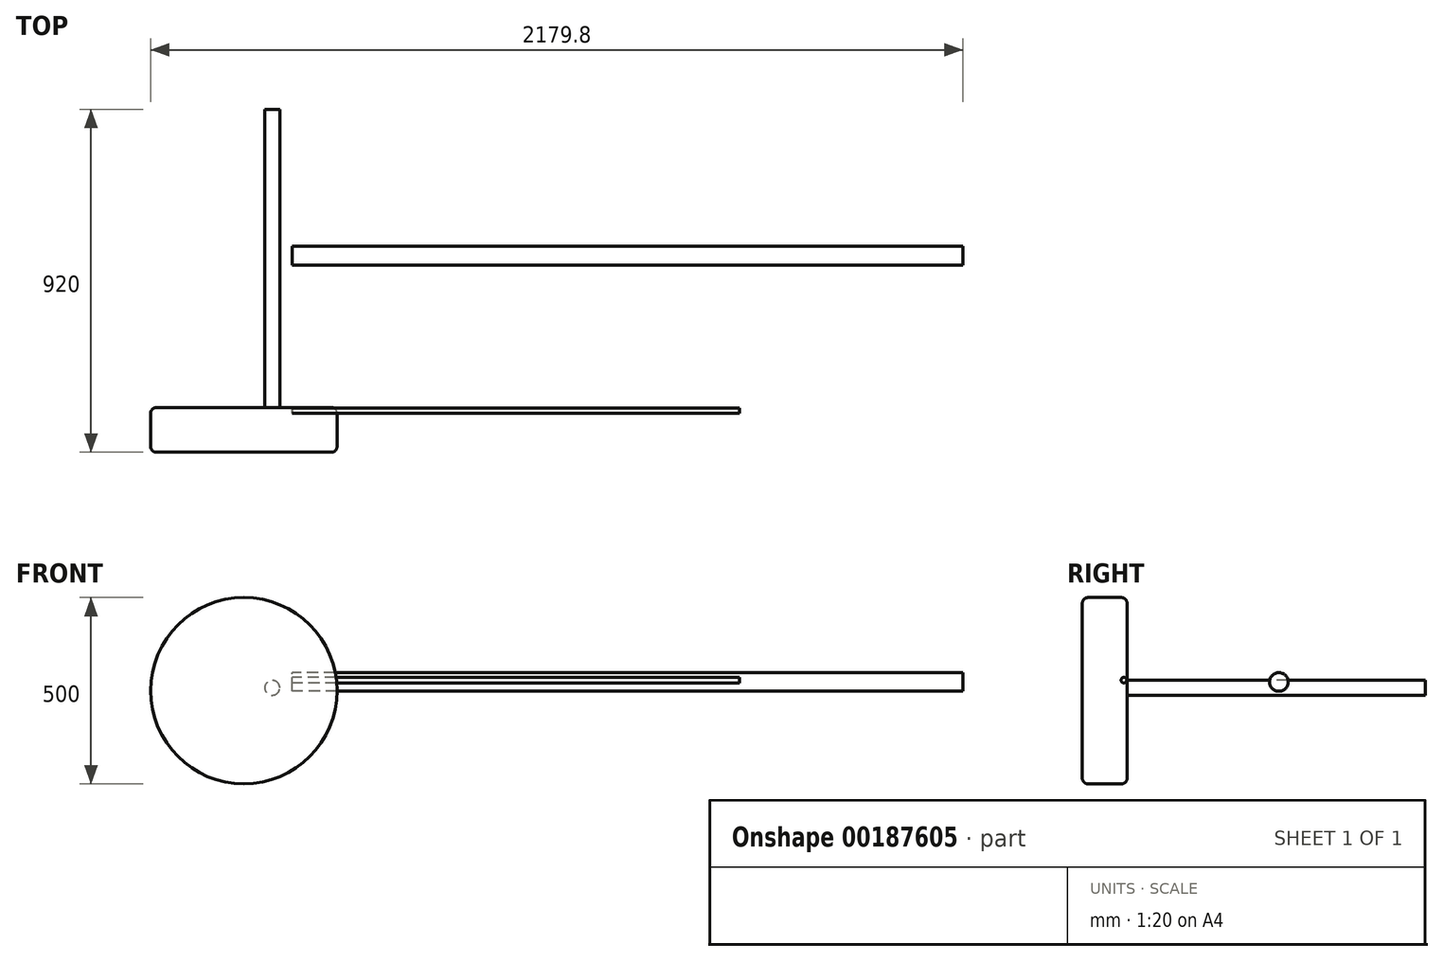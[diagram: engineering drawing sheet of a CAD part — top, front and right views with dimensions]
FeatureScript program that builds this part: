
annotation { "Feature Type Name" : "Feature", "Feature Type Description" : "" }
export const myFeature = defineFeature(function(context is Context, id is Id, definition is map)
    precondition{}
    {
        {
            var Q0;
            Q0=qCreatedBy(makeId("Front.planeOp"),FACE);
            var sketch = newSketch(context, id + "F0", { "sketchPlane" : qUnion([Q0])});
            skCircle(sketch, "E0", {"center": v(-129.8, -23.54) * mm, "radius": 250 * mm});
            skSolve(sketch);
        }
        {
            var Q0;
            Q0=makeQuery(id+"F0.imprint","IMPRINT",FACE,{"disambiguationData":[TD([[makeQuery(id+"F0.imprint","IMPRINT",EDGE,{"derivedFrom":sQuery(id+"F0.wireOp",EDGE,"E0")}),1.0]])]});
            extrude(context, id + "F1", {"entities" : qUnion([Q0]), "depth" : 120 * mm});
        }
        {
            var Q0;
            Q0=makeQuery(id+"F1.opExtrude","CAP_EDGE",EDGE,{"disambiguationData":[OSD([sQuery(id+"F0.wireOp",EDGE,"E0")])],"isStart":true});
            var Q1;
            Q1=makeQuery(id+"F1.opExtrude","SWEPT_FACE",FACE,{"disambiguationData":[OSD([sQuery(id+"F0.wireOp",EDGE,"E0")])]});
            fillet(context, id + "F2", {"entities" : qUnion([Q0, Q1]), "radius" : 15 * mm, "tangentPropagation" : true, "allowEdgeOverflow" : false});
        }
        {
            var Q0;
            Q0=qCreatedBy(makeId("Front.planeOp"),FACE);
            var sketch = newSketch(context, id + "F3", { "sketchPlane" : qUnion([Q0])});
            skCircle(sketch, "E1", {"center": v(-53.57, -15.6) * mm, "radius": 20 * mm});
            skSolve(sketch);
        }
        {
            var Q0;
            Q0=makeQuery(id+"F3.imprint","IMPRINT",FACE,{"disambiguationData":[TD([[makeQuery(id+"F3.imprint","IMPRINT",EDGE,{"derivedFrom":sQuery(id+"F3.wireOp",EDGE,"E1")}),1.0]])]});
            extrude(context, id + "F4", {"entities" : qUnion([Q0]), "oppositeDirection" : true, "depth" : 800 * mm});
        }
        {
            var Q0;
            Q0=qCreatedBy(makeId("Right.planeOp"),FACE);
            var sketch = newSketch(context, id + "F5", { "sketchPlane" : qUnion([Q0])});
            skCircle(sketch, "E2", {"center": v(-8.47, 4.92) * mm, "radius": 7.5 * mm});
            skSolve(sketch);
        }
        {
            var Q0;
            Q0=makeQuery(id+"F5.imprint","IMPRINT",FACE,{"disambiguationData":[TD([[makeQuery(id+"F5.imprint","IMPRINT",EDGE,{"derivedFrom":sQuery(id+"F5.wireOp",EDGE,"E2")}),1.0]])]});
            extrude(context, id + "F6", {"entities" : qUnion([Q0]), "depth" : 1200 * mm});
        }
        {
            var Q0;
            Q0=qCreatedBy(makeId("Right.planeOp"),FACE);
            var sketch = newSketch(context, id + "F7", { "sketchPlane" : qUnion([Q0])});
            skCircle(sketch, "E3", {"center": v(407.4, 0) * mm, "radius": 25 * mm});
            skSolve(sketch);
        }
        {
            var Q0;
            Q0=makeQuery(id+"F7.imprint","IMPRINT",FACE,{"disambiguationData":[TD([[makeQuery(id+"F7.imprint","IMPRINT",EDGE,{"derivedFrom":sQuery(id+"F7.wireOp",EDGE,"E3")}),1.0]])]});
            extrude(context, id + "F8", {"entities" : qUnion([Q0]), "depth" : 1800 * mm});
        }
    });
